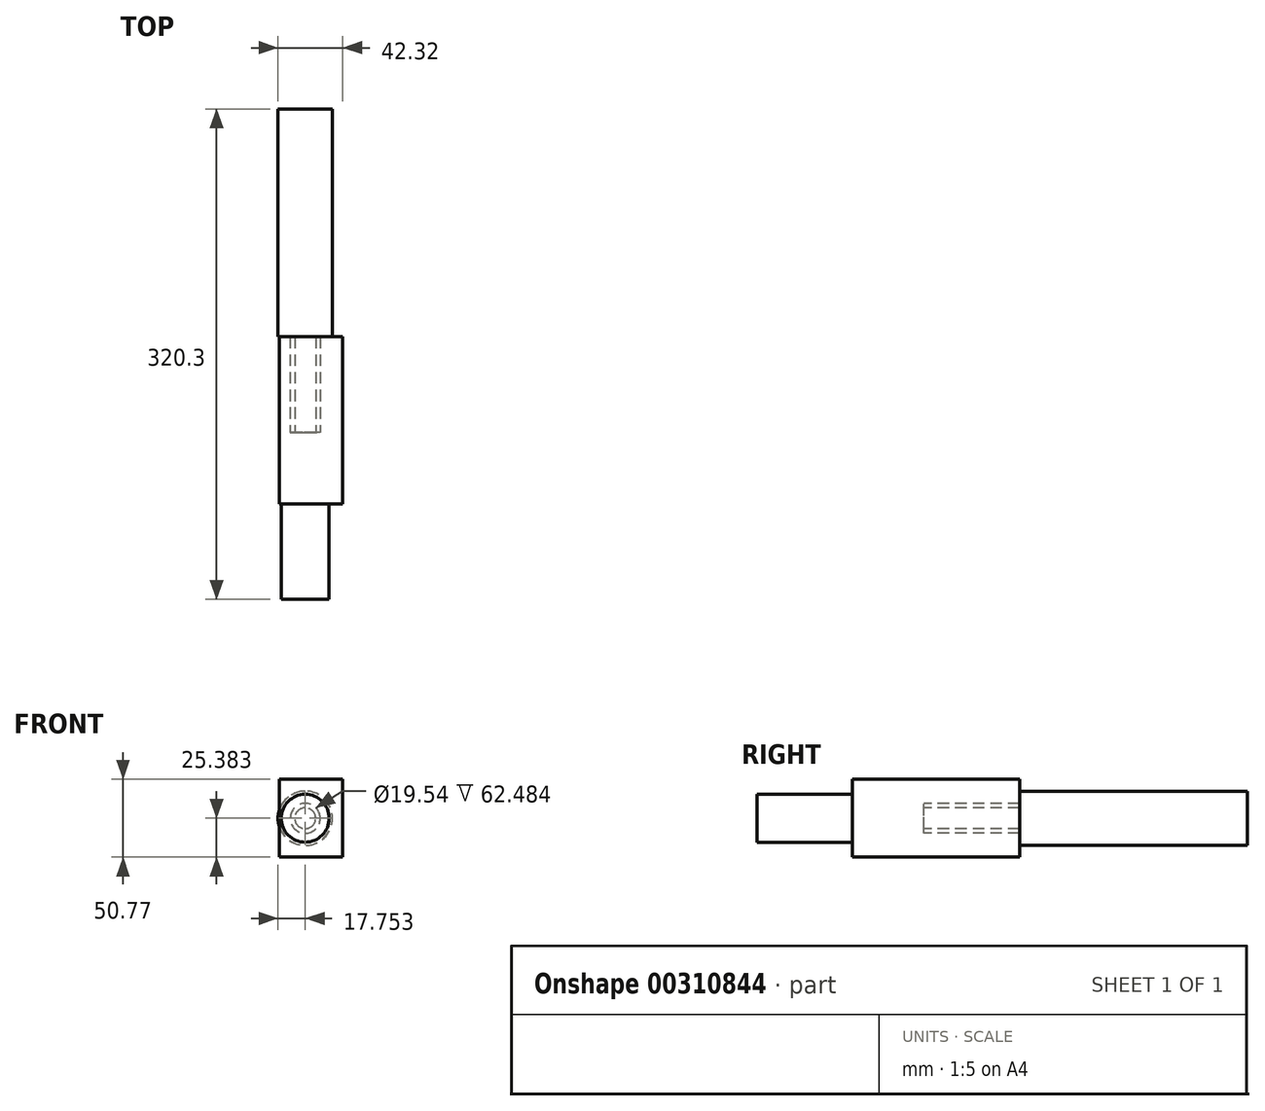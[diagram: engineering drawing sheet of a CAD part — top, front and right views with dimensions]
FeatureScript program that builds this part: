
annotation { "Feature Type Name" : "Feature", "Feature Type Description" : "" }
export const myFeature = defineFeature(function(context is Context, id is Id, definition is map)
    precondition{}
    {
        {
            var Q0;
            Q0=qCreatedBy(makeId("Front.planeOp"),FACE);
            var sketch = newSketch(context, id + "F0", { "sketchPlane" : qUnion([Q0])});
            skLineSegment(sketch, "E0.bottom", {"start": v(-108.3, 0) * mm, "end": v(-66.8, 0) * mm});
            skLineSegment(sketch, "E0.top", {"start": v(-108.3, -50.77) * mm, "end": v(-66.8, -50.77) * mm});
            skLineSegment(sketch, "E0.left", {"start": v(-108.3, 0) * mm, "end": v(-108.3, -50.77) * mm});
            skLineSegment(sketch, "E0.right", {"start": v(-66.8, 0) * mm, "end": v(-66.8, -50.77) * mm});
            skCircle(sketch, "E1", {"center": v(-91.38, -25.39) * mm, "radius": 9.77 * mm});
            skPoint(sketch, "E1.centerSnap0", {"position": v(-108.3, -25.39) * mm});
            skSolve(sketch);
        }
        {
            var Q0;
            Q0=qSketchRegion(id+"F0",true);
            extrude(context, id + "F1", {"entities" : qUnion([Q0]), "oppositeDirection" : true, "depth" : 62.48 * mm});
        }
        {
            var Q0;
            Q0=makeQuery(id+"F1.opExtrude","CAP_FACE",FACE,{"disambiguationData":[OSD([sQuery(id+"F0.wireOp",EDGE,"E0.bottom"),sQuery(id+"F0.wireOp",EDGE,"E0.top"),sQuery(id+"F0.wireOp",EDGE,"E0.left"),sQuery(id+"F0.wireOp",EDGE,"E0.right"),sQuery(id+"F0.wireOp",EDGE,"E1")])],"isStart":true});
            var sketch = newSketch(context, id + "F2", { "sketchPlane" : qUnion([Q0])});
            skCircle(sketch, "E2", {"center": v(-91.38, -25.39) * mm, "radius": 15.64 * mm});
            skSolve(sketch);
        }
        {
            var Q0;
            Q0=qSketchRegion(id+"F2",true);
            var Q1;
            Q1=makeQuery(id+"F1.opExtrude","CAP_FACE",FACE,{"disambiguationData":[OSD([sQuery(id+"F0.wireOp",EDGE,"E0.bottom"),sQuery(id+"F0.wireOp",EDGE,"E0.top"),sQuery(id+"F0.wireOp",EDGE,"E0.left"),sQuery(id+"F0.wireOp",EDGE,"E0.right"),sQuery(id+"F0.wireOp",EDGE,"E1")])],"isStart":false});
            extrude(context, id + "F3", {"entities" : qUnion([Q0, Q1]), "operationType" : NewBodyOperationType.ADD, "depth" : 108.97 * mm});
        }
        {
            var Q0;
            Q0=makeQuery(id+"F1.opExtrude","CAP_FACE",FACE,{"disambiguationData":[OSD([sQuery(id+"F0.wireOp",EDGE,"E0.bottom"),sQuery(id+"F0.wireOp",EDGE,"E0.top"),sQuery(id+"F0.wireOp",EDGE,"E0.left"),sQuery(id+"F0.wireOp",EDGE,"E0.right"),sQuery(id+"F0.wireOp",EDGE,"E1")])],"isStart":false});
            var sketch = newSketch(context, id + "F4", { "sketchPlane" : qUnion([Q0])});
            skCircle(sketch, "E3", {"center": v(91.38, -25.39) * mm, "radius": 17.75 * mm});
            skSolve(sketch);
        }
        {
            var Q0;
            Q0=qSketchRegion(id+"F4",true);
            extrude(context, id + "F5", {"entities" : qUnion([Q0]), "operationType" : NewBodyOperationType.ADD, "depth" : 148.84 * mm});
        }
        {
            var Q0;
            Q0=makeQuery(id+"F3.opExtrude","CAP_FACE",FACE,{"disambiguationData":[OSD([sQuery(id+"F2.wireOp",EDGE,"E2")])],"isStart":false});
            var sketch = newSketch(context, id + "F6", { "sketchPlane" : qUnion([Q0])});
            skCircle(sketch, "E4", {"center": v(-91.38, -25.39) * mm, "radius": 6.83 * mm});
            skSolve(sketch);
        }
        {
            var Q0;
            Q0 = qSketchRegion(id + "F6", true);
            extrude(context, id + "F7", {"entities" : qUnion([Q0]), "operationType" : NewBodyOperationType.ADD, "oppositeDirection" : true, "depth" : 248.92 * mm});
        }
    });
